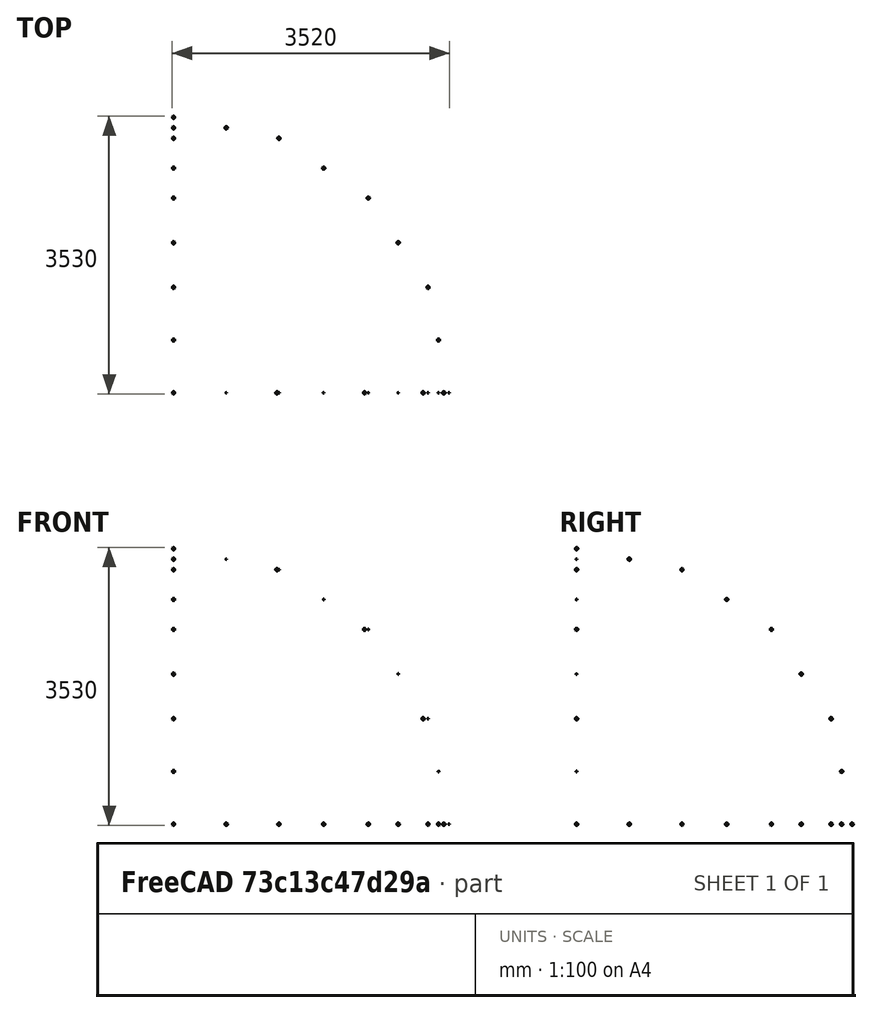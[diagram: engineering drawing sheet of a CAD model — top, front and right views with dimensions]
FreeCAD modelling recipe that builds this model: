
FCSTD DOCUMENT  (FreeCAD 0.20R29603 (Git))
Label: z_pointing
License: All rights reserved
LicenseURL: http://en.wikipedia.org/wiki/All_rights_reserved
objects: Part::Sphere×29, Part::Part2DObjectPython×27
note: 56 computed .brp shape members not serialized (recipe doc carries the construction recipe); baked Part::Feature solids carry a one-line shape summary decoded from their .brp

FEATURE [Part::Part2DObjectPython] Line  # Draft 2D object (typed FeaturePython)
  Area = 0
  ChamferSize = 0
  Closed = false
  End = (3233.58,0,1339.39)
  FilletRadius = 0
  Length = 1365.63
  MakeFace = false
  Points = (2) [(3500,0,0),(3233.58,0,1339.39)]
  Start = (3500,0,0)
  Subdivisions = 0
FEATURE [Part::Part2DObjectPython] Line002  # Draft 2D object (typed FeaturePython)
  Area = 0
  ChamferSize = 0
  Closed = false
  End = (3233.58,1339.39,0)
  FilletRadius = 0
  Length = 1365.63
  MakeFace = false
  Points = (2) [(3500,0,0),(3233.58,1339.39,0)]
  Start = (3500,0,0)
  Subdivisions = 0
FEATURE [Part::Part2DObjectPython] Line003  # Draft 2D object (typed FeaturePython)
  Area = 0
  ChamferSize = 0
  Closed = false
  End = (3171.45,630.84,1339.39)
  FilletRadius = 0
  Length = 1261.68
  MakeFace = false
  Placement = pos=(0,0,0) rot=(0,0,1;6.08684rad)
  Points = (2) [(3233.58,0,1339.39),(2987.44,1237.44,1339.39)]
  Start = (3171.45,-630.84,1339.39)
  Subdivisions = 0
FEATURE [Part::Part2DObjectPython] Line004  # Draft 2D object (typed FeaturePython)
  Area = 0
  ChamferSize = 0
  Closed = false
  End = (2427.32,482.824,2474.87)
  FilletRadius = 0
  Length = 965.648
  MakeFace = false
  Placement = pos=(0,0,0) rot=(0,0,1;6.08684rad)
  Points = (2) [(2474.87,0,2474.87),(2286.49,947.093,2474.87)]
  Start = (2427.32,-482.824,2474.87)
  Subdivisions = 0
FEATURE [Part::Part2DObjectPython] Line005  # Draft 2D object (typed FeaturePython)
  Area = 0
  ChamferSize = 0
  Closed = false
  End = (1313.66,261.302,3233.58)
  FilletRadius = 0
  Length = 522.605
  MakeFace = false
  Placement = pos=(0,0,0) rot=(0,0,1;6.08684rad)
  Points = (2) [(1339.39,0,3233.58),(1237.44,512.563,3233.58)]
  Start = (1313.66,-261.302,3233.58)
  Subdivisions = 0
FEATURE [Part::Part2DObjectPython] Line006  # Draft 2D object (typed FeaturePython)
  Area = 0
  ChamferSize = 0
  Closed = false
  End = (0.0092388,0.00382683,3500)
  FilletRadius = 0
  Length = 0.00390181
  MakeFace = false
  Points = (2) [(0.01,0,3500),(0.0092388,0.00382683,3500)]
  Start = (0.01,0,3500)
  Subdivisions = 0
FEATURE [Part::Part2DObjectPython] Line007  # Draft 2D object (typed FeaturePython)
  Area = 0
  ChamferSize = 0
  Closed = false
  End = (2474.87,0,2474.87)
  FilletRadius = 0
  Length = 1365.63
  MakeFace = false
  Placement = pos=(0,0,0) rot=(0,1,0;5.89049rad)
  Points = (2) [(3500,0,2.27374e-13),(3233.58,0,1339.39)]
  Start = (3233.58,0,1339.39)
  Subdivisions = 0
FEATURE [Part::Part2DObjectPython] Line008  # Draft 2D object (typed FeaturePython)
  Area = 0
  ChamferSize = 0
  Closed = false
  End = (-6.821e-13,0,3500)
  FilletRadius = 0
  Length = 1365.63
  MakeFace = false
  Placement = pos=(0,0,0) rot=(0,-1,0;1.1781rad)
  Points = (2) [(3500,0,-4.54747e-13),(3233.58,0,1339.39)]
  Start = (1339.39,0,3233.58)
  Subdivisions = 0
FEATURE [Part::Part2DObjectPython] Line009  # Draft 2D object (typed FeaturePython)
  Area = 0
  ChamferSize = 0
  Closed = false
  End = (1339.39,0,3233.58)
  FilletRadius = 0
  Length = 1365.63
  MakeFace = false
  Placement = pos=(0,0,0) rot=(0,1,0;5.49779rad)
  Points = (2) [(3500,0,-9.09495e-13),(3233.58,0,1339.39)]
  Start = (2474.87,0,2474.87)
  Subdivisions = 0
FEATURE [Part::Part2DObjectPython] Line010  # Draft 2D object (typed FeaturePython)
  Area = 0
  ChamferSize = 0
  Closed = false
  End = (-1.5916e-12,-1.5916e-12,3500)
  FilletRadius = 0
  Length = 3500
  MakeFace = true
  Placement = pos=(0,0,0) rot=(0.799257,0.125953,0.587643;1.11975rad)
  Points = (2) [(0,0,0),(530.542,2663.76,2207.47)]
  Start = (0,0,0)
  Subdivisions = 0
FEATURE [Part::Part2DObjectPython] Line011  # Draft 2D object (typed FeaturePython)
  Area = 0
  ChamferSize = 0
  Closed = false
  End = (3500,1.137e-13,0)
  FilletRadius = 0
  Length = 3500
  MakeFace = true
  Placement = pos=(0,0,0) rot=(0.799257,0.125953,0.587643;1.11975rad)
  Points = (2) [(0,0,0),(2786.9,-1652.3,1324.04)]
  Start = (0,0,0)
  Subdivisions = 0
FEATURE [Part::Part2DObjectPython] Line012  # Draft 2D object (typed FeaturePython)
  Area = 0
  ChamferSize = 0
  Closed = false
  End = (2474.87,2474.87,0)
  FilletRadius = 0
  Length = 1365.63
  MakeFace = false
  Placement = pos=(0,0,0) rot=(0,0,1;0.392699rad)
  Points = (2) [(3500,0,0),(3233.58,1339.39,0)]
  Start = (3233.58,1339.39,0)
  Subdivisions = 0
FEATURE [Part::Part2DObjectPython] Line013  # Draft 2D object (typed FeaturePython)
  Area = 0
  ChamferSize = 0
  Closed = false
  End = (1339.39,3233.58,0)
  FilletRadius = 0
  Length = 1365.63
  MakeFace = false
  Placement = pos=(0,0,0) rot=(0,0,1;0.785398rad)
  Points = (2) [(3500,-2.27374e-13,0),(3233.58,1339.39,0)]
  Start = (2474.87,2474.87,0)
  Subdivisions = 0
FEATURE [Part::Part2DObjectPython] Line014  # Draft 2D object (typed FeaturePython)
  Area = 0
  ChamferSize = 0
  Closed = false
  End = (-4.7748e-12,3500,0)
  FilletRadius = 0
  Length = 1365.63
  MakeFace = false
  Placement = pos=(0,0,0) rot=(0,0,1;1.1781rad)
  Points = (2) [(3500,0,0),(3233.58,1339.39,0)]
  Start = (1339.39,3233.58,0)
  Subdivisions = 0
FEATURE [Part::Part2DObjectPython] Line015  # Draft 2D object (typed FeaturePython)
  Area = 0
  ChamferSize = 0
  Closed = false
  End = (-4.917e-12,3500,5.68e-14)
  FilletRadius = 0
  Length = 3500
  MakeFace = true
  Placement = pos=(0,0,0) rot=(0.23465,0.959688,0.154721;0.514623rad)
  Points = (2) [(0,0,0),(368.626,3464.19,-336.926)]
  Start = (0,0,0)
  Subdivisions = 0
FEATURE [Part::Part2DObjectPython] Line016  # Draft 2D object (typed FeaturePython)
  Area = 0
  ChamferSize = 0
  Closed = false
  End = (-1.816e-13,-1.1369e-12,3500)
  FilletRadius = 0
  Length = 1365.63
  MakeFace = false
  Placement = pos=(0,0,0) rot=(0.485653,-0.485653,0.726831;1.88458rad)
  Points = (2) [(3500,2.967e-13,-9.09495e-13),(3233.58,-1.26643e-14,1339.39)]
  Start = (-2.335e-12,1339.39,3233.58)
  Subdivisions = 0
FEATURE [Part::Part2DObjectPython] Line017  # Draft 2D object (typed FeaturePython)
  Area = 0
  ChamferSize = 0
  Closed = false
  End = (-1.781e-12,1339.39,3233.58)
  FilletRadius = 0
  Length = 1365.63
  MakeFace = false
  Placement = pos=(0,0,0) rot=(0.357407,-0.357407,0.862856;1.71777rad)
  Points = (2) [(3500,1.7158e-14,1.13687e-12),(3233.58,1.01678e-13,1339.39)]
  Start = (-3.3144e-12,2474.87,2474.87)
  Subdivisions = 0
FEATURE [Part::Part2DObjectPython] Line018  # Draft 2D object (typed FeaturePython)
  Area = 0
  ChamferSize = 0
  Closed = false
  End = (-3.5495e-12,2474.87,2474.87)
  FilletRadius = 0
  Length = 1365.63
  MakeFace = false
  Placement = pos=(0,0,0) rot=(0.19148,-0.19148,0.962637;1.60887rad)
  Points = (2) [(3500,-1.21632e-14,4.54747e-13),(3233.58,-2.24415e-14,1339.39)]
  Start = (-4.6548e-12,3233.58,1339.39)
  Subdivisions = 0
FEATURE [Part::Part2DObjectPython] Line019  # Draft 2D object (typed FeaturePython)
  Area = 0
  ChamferSize = 0
  Closed = false
  End = (-4.4875e-12,3233.58,1339.39)
  FilletRadius = 0
  Length = 1365.63
  MakeFace = false
  Placement = pos=(0,0,0) rot=(0,0,1;1.5708rad)
  Points = (2) [(3500,0,0),(3233.58,0,1339.39)]
  Start = (-4.8572e-12,3500,0)
  Subdivisions = 0
FEATURE [Part::Sphere] Sphere  label="Сфера"
  Angle1 = -90
  Angle2 = 90
  Angle3 = 360
  AttacherType = Attacher::AttachEngine3D
  Placement = pos=(3500,0,0) rot=(0,0,1;0rad)
  Radius = 5
FEATURE [Part::Sphere] Sphere001  label="Сфера001"
  Angle1 = -90
  Angle2 = 90
  Angle3 = 360
  AttacherType = Attacher::AttachEngine3D
  Radius = 15
FEATURE [Part::Sphere] Sphere002  label="Сфера002"
  Angle1 = -90
  Angle2 = 90
  Angle3 = 360
  AttacherType = Attacher::AttachEngine3D
  Placement = pos=(-1.1369e-12,-1.3642e-12,3500) rot=(0,0,1;0rad)
  Radius = 15
FEATURE [Part::Sphere] Sphere003  label="Сфера003"
  Angle1 = -90
  Angle2 = 90
  Angle3 = 360
  AttacherType = Attacher::AttachEngine3D
  Placement = pos=(1339.39,-1.3642e-12,3233.58) rot=(0,0,1;0rad)
  Radius = 5
FEATURE [Part::Sphere] Sphere004  label="Сфера004"
  Angle1 = -90
  Angle2 = 90
  Angle3 = 360
  AttacherType = Attacher::AttachEngine3D
  Placement = pos=(2474.87,-1.3642e-12,2474.87) rot=(0,0,1;0rad)
  Radius = 5
FEATURE [Part::Sphere] Sphere005  label="Сфера005"
  Angle1 = -90
  Angle2 = 90
  Angle3 = 360
  AttacherType = Attacher::AttachEngine3D
  Placement = pos=(3233.58,-1.3642e-12,1339.39) rot=(0,0,1;0rad)
  Radius = 5
FEATURE [Part::Sphere] Sphere006  label="Сфера006"
  Angle1 = -90
  Angle2 = 90
  Angle3 = 360
  AttacherType = Attacher::AttachEngine3D
  Placement = pos=(4.5475e-12,3500,3.1832e-12) rot=(0,0,1;0rad)
  Radius = 15
FEATURE [Part::Sphere] Sphere007  label="Сфера007"
  Angle1 = -90
  Angle2 = 90
  Angle3 = 360
  AttacherType = Attacher::AttachEngine3D
  Placement = pos=(4.9019e-12,3233.58,1339.39) rot=(0,0,1;0rad)
  Radius = 15
FEATURE [Part::Sphere] Sphere008  label="Сфера008"
  Angle1 = -90
  Angle2 = 90
  Angle3 = 360
  AttacherType = Attacher::AttachEngine3D
  Placement = pos=(6.1161e-12,2474.87,2474.87) rot=(0,0,1;0rad)
  Radius = 15
FEATURE [Part::Sphere] Sphere009  label="Сфера009"
  Angle1 = -90
  Angle2 = 90
  Angle3 = 360
  AttacherType = Attacher::AttachEngine3D
  Placement = pos=(8.7464e-12,1339.39,3233.58) rot=(0,0,1;0rad)
  Radius = 15
FEATURE [Part::Sphere] Sphere010  label="Сфера010"
  Angle1 = -90
  Angle2 = 90
  Angle3 = 360
  AttacherType = Attacher::AttachEngine3D
  Placement = pos=(1339.39,3233.58,-2.7285e-12) rot=(0,0,1;0rad)
  Radius = 15
FEATURE [Part::Sphere] Sphere011  label="Сфера011"
  Angle1 = -90
  Angle2 = 90
  Angle3 = 360
  AttacherType = Attacher::AttachEngine3D
  Placement = pos=(2474.87,2474.87,-2.728e-12) rot=(0,0,1;0rad)
  Radius = 15
FEATURE [Part::Sphere] Sphere012  label="Сфера012"
  Angle1 = -90
  Angle2 = 90
  Angle3 = 360
  AttacherType = Attacher::AttachEngine3D
  Placement = pos=(3233.58,1339.39,-2.728e-12) rot=(0,0,1;0rad)
  Radius = 15
FEATURE [Part::Sphere] Sphere013  label="Сфера013"
  Angle1 = -90
  Angle2 = 90
  Angle3 = 360
  AttacherType = Attacher::AttachEngine3D
  Placement = pos=(3366.79,669.696,0) rot=(0,0,1;0rad)
  Radius = 15
FEATURE [Part::Sphere] Sphere014  label="Сфера014"
  Angle1 = -90
  Angle2 = 90
  Angle3 = 360
  AttacherType = Attacher::AttachEngine3D
  Placement = pos=(2854.23,1907.13,0) rot=(0,0,1;0rad)
  Radius = 15
FEATURE [Part::Sphere] Sphere015  label="Сфера015"
  Angle1 = -90
  Angle2 = 90
  Angle3 = 360
  AttacherType = Attacher::AttachEngine3D
  Placement = pos=(1907.13,2854.23,0) rot=(0,0,1;0rad)
  Radius = 15
FEATURE [Part::Sphere] Sphere016  label="Сфера016"
  Angle1 = -90
  Angle2 = 90
  Angle3 = 360
  AttacherType = Attacher::AttachEngine3D
  Placement = pos=(669.696,3366.79,0) rot=(0,0,1;0rad)
  Radius = 15
FEATURE [Part::Sphere] Sphere017  label="Сфера017"
  Angle1 = -90
  Angle2 = 90
  Angle3 = 360
  AttacherType = Attacher::AttachEngine3D
  Placement = pos=(-4.3201e-12,3366.79,669.696) rot=(0,0,1;0rad)
  Radius = 15
FEATURE [Part::Sphere] Sphere018  label="Сфера018"
  Angle1 = -90
  Angle2 = 90
  Angle3 = 360
  AttacherType = Attacher::AttachEngine3D
  Placement = pos=(-4.6636e-12,2854.23,1907.13) rot=(0,0,1;0rad)
  Radius = 15
FEATURE [Part::Sphere] Sphere019  label="Сфера019"
  Angle1 = -90
  Angle2 = 90
  Angle3 = 360
  AttacherType = Attacher::AttachEngine3D
  Placement = pos=(-2.188e-12,1907.13,2854.23) rot=(0,0,1;0rad)
  Radius = 15
FEATURE [Part::Sphere] Sphere020  label="Сфера020"
  Angle1 = -90
  Angle2 = 90
  Angle3 = 360
  AttacherType = Attacher::AttachEngine3D
  Placement = pos=(-1.9253e-12,669.696,3366.79) rot=(0,0,1;0rad)
  Radius = 15
FEATURE [Part::Sphere] Sphere021  label="Сфера021"
  Angle1 = -90
  Angle2 = 90
  Angle3 = 360
  AttacherType = Attacher::AttachEngine3D
  Placement = pos=(669.696,-1.137e-13,3366.79) rot=(0,0,1;0rad)
  Radius = 5
FEATURE [Part::Sphere] Sphere022  label="Сфера022"
  Angle1 = -90
  Angle2 = 90
  Angle3 = 360
  AttacherType = Attacher::AttachEngine3D
  Placement = pos=(1907.13,-1.14e-13,2854.23) rot=(0,0,1;0rad)
  Radius = 5
FEATURE [Part::Sphere] Sphere023  label="Сфера023"
  Angle1 = -90
  Angle2 = 90
  Angle3 = 360
  AttacherType = Attacher::AttachEngine3D
  Placement = pos=(2854.23,-1.14e-13,1907.13) rot=(0,0,1;0rad)
  Radius = 5
FEATURE [Part::Sphere] Sphere024  label="Сфера024"
  Angle1 = -90
  Angle2 = 90
  Angle3 = 360
  AttacherType = Attacher::AttachEngine3D
  Placement = pos=(3366.79,-1.14e-13,669.696) rot=(0,0,1;0rad)
  Radius = 5
FEATURE [Part::Part2DObjectPython] Line020  # Draft 2D object (typed FeaturePython)
  Area = 0
  ChamferSize = 0
  Closed = false
  End = (3432.75,682.816,0)
  FilletRadius = 0
  Length = 1365.63
  MakeFace = false
  Placement = pos=(0,0,0) rot=(0,0,1;6.08684rad)
  Points = (2) [(3500,0,0),(3233.58,1339.39,0)]
  Start = (3432.75,-682.816,0)
  Subdivisions = 0
FEATURE [Part::Part2DObjectPython] Line023  # Draft 2D object (typed FeaturePython)
  Area = 0
  ChamferSize = 0
  Closed = false
  End = (1313.66,8.491e-13,3233.58)
  FilletRadius = 0
  Length = 1325.4
  MakeFace = true
  Placement = pos=(14.7118,-1.3678e-12,3497.07) rot=(0.686613,0.703228,-0.184481;1.23965rad)
  Points = (2) [(0,0,0),(1033.35,501.861,661.064)]
  Start = (14.7118,-1.3678e-12,3497.07)
  Subdivisions = 0
FEATURE [Part::Part2DObjectPython] Line025  # Draft 2D object (typed FeaturePython)
  Area = 0
  ChamferSize = 0
  Closed = false
  End = (2427.32,1.3074e-12,2474.87)
  FilletRadius = 0
  Length = 1347.55
  MakeFace = true
  Placement = pos=(1313.66,6.253e-13,3233.58) rot=(0.686613,0.703228,-0.184481;1.23965rad)
  Points = (2) [(0,0,0),(1285.82,130.976,381.305)]
  Start = (1313.66,6.253e-13,3233.58)
  Subdivisions = 0
FEATURE [Part::Part2DObjectPython] Line027  # Draft 2D object (typed FeaturePython)
  Area = 0
  ChamferSize = 0
  Closed = false
  End = (3171.45,2.2595e-12,1339.39)
  FilletRadius = 0
  Length = 1357.59
  MakeFace = true
  Placement = pos=(2427.32,1.1937e-12,2474.87) rot=(0.686613,0.703228,-0.184481;1.23965rad)
  Points = (2) [(0,0,0),(1330.87,-265.566,35.9882)]
  Start = (2427.32,1.1937e-12,2474.87)
  Subdivisions = 0
FEATURE [Part::Part2DObjectPython] Line029  # Draft 2D object (typed FeaturePython)
  Area = 0
  ChamferSize = 0
  Closed = false
  End = (3432.75,2.7853e-12,-1.5916e-12)
  FilletRadius = 0
  Length = 1364.64
  MakeFace = true
  Placement = pos=(3171.45,1.4779e-12,1339.39) rot=(0.686613,0.703228,-0.184481;1.23965rad)
  Points = (2) [(0,0,0),(1173.31,-621.678,-314.807)]
  Start = (3171.45,1.4779e-12,1339.39)
  Subdivisions = 0
FEATURE [Part::Sphere] Sphere025  label="Сфера025"
  Angle1 = -90
  Angle2 = 90
  Angle3 = 360
  AttacherType = Attacher::AttachEngine3D
  Placement = pos=(1313.66,6.253e-13,3233.58) rot=(0,0,1;0rad)
  Radius = 15
FEATURE [Part::Sphere] Sphere026  label="Сфера026"
  Angle1 = -90
  Angle2 = 90
  Angle3 = 360
  AttacherType = Attacher::AttachEngine3D
  Placement = pos=(2427.32,1.1934e-12,2474.87) rot=(0,0,1;0rad)
  Radius = 15
FEATURE [Part::Sphere] Sphere027  label="Сфера027"
  Angle1 = -90
  Angle2 = 90
  Angle3 = 360
  AttacherType = Attacher::AttachEngine3D
  Placement = pos=(3171.45,1.4772e-12,1339.39) rot=(0,0,1;0rad)
  Radius = 15
FEATURE [Part::Sphere] Sphere028  label="Сфера028"
  Angle1 = -90
  Angle2 = 90
  Angle3 = 360
  AttacherType = Attacher::AttachEngine3D
  Placement = pos=(3432.75,-1.913e-13,0) rot=(0,0,1;0rad)
  Radius = 15
FEATURE [Part::Part2DObjectPython] Line030  # Draft 2D object (typed FeaturePython)
  Area = 0
  ChamferSize = 0
  Closed = false
  End = (1313.66,-4.547e-13,3233.58)
  FilletRadius = 0
  Length = 3490.23
  MakeFace = true
  Placement = pos=(0,0,0) rot=(0.985079,0.096039,0.142817;1.22271rad)
  Points = (2) [(0,0,0),(1295.84,2929.04,1386.8)]
  Start = (0,0,0)
  Subdivisions = 0
FEATURE [Part::Part2DObjectPython] Line033  # Draft 2D object (typed FeaturePython)
  Area = 0
  ChamferSize = 0
  Closed = false
  End = (2427.32,2.274e-13,2474.87)
  FilletRadius = 0
  Length = 3466.54
  MakeFace = true
  Placement = pos=(0,0,0) rot=(0.985079,0.096039,0.142817;1.22271rad)
  Points = (2) [(0,0,0),(2385.93,2139.54,1321.59)]
  Start = (0,0,0)
  Subdivisions = 0
FEATURE [Part::Part2DObjectPython] Line035  # Draft 2D object (typed FeaturePython)
  Area = 0
  ChamferSize = 0
  Closed = false
  End = (3171.45,6.821e-13,1339.39)
  FilletRadius = 0
  Length = 3442.68
  MakeFace = true
  Placement = pos=(0,0,0) rot=(0.985079,0.096039,0.142817;1.22271rad)
  Points = (2) [(0,0,0),(3112.79,1024.3,1055.17)]
  Start = (0,0,0)
  Subdivisions = 0
